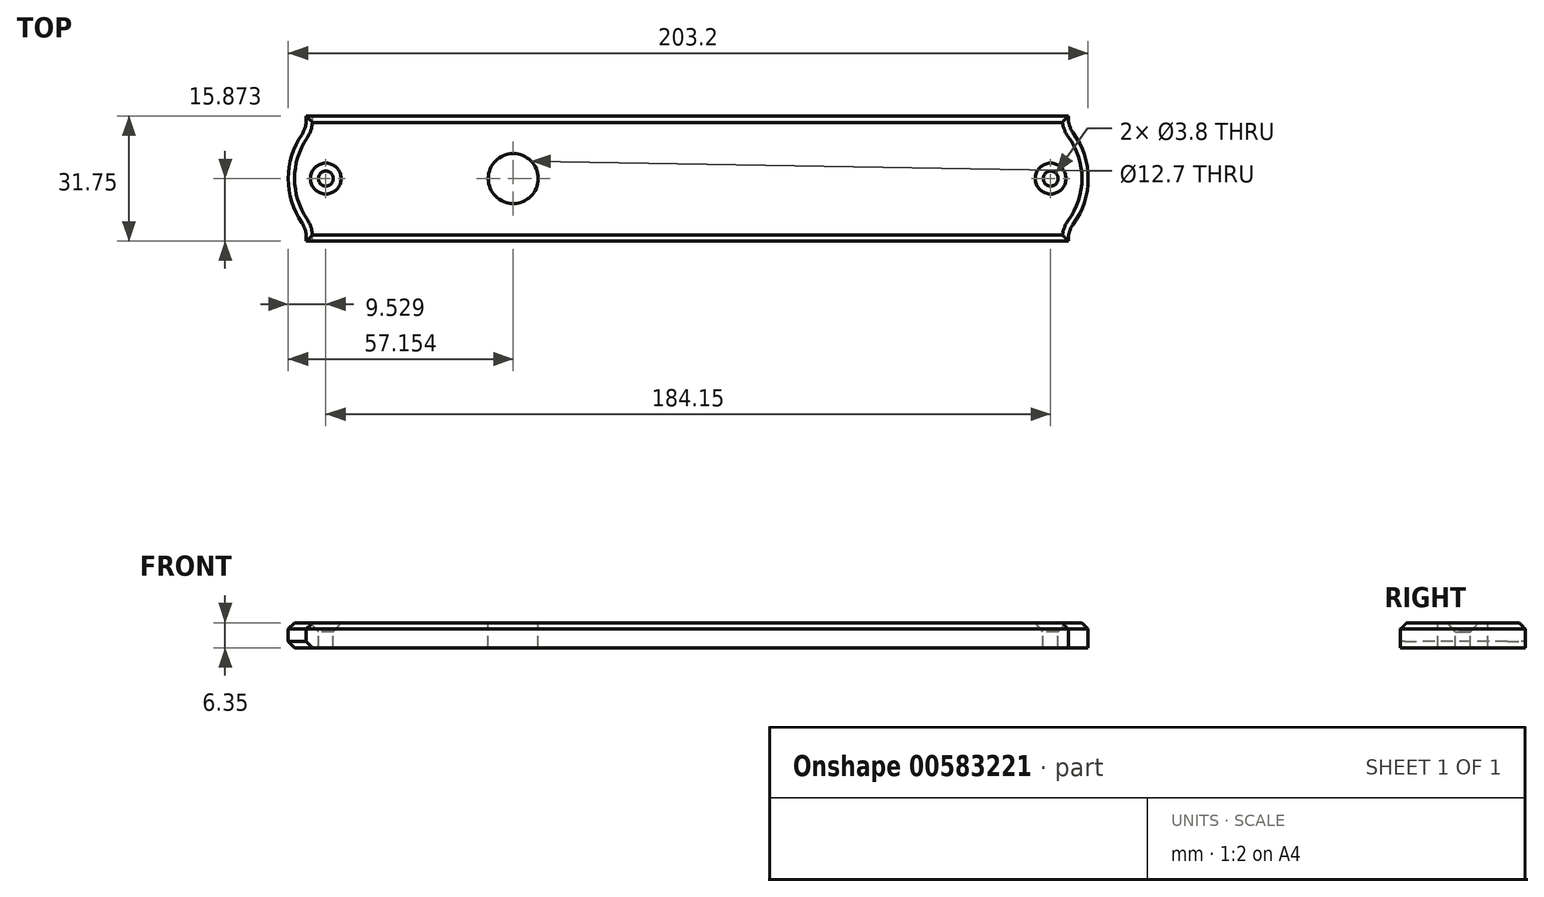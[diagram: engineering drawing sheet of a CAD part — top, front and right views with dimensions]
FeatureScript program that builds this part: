
annotation { "Feature Type Name" : "Feature", "Feature Type Description" : "" }
export const myFeature = defineFeature(function(context is Context, id is Id, definition is map)
    precondition{}
    {
        {
            var Q0;
            Q0=qCreatedBy(makeId("Top.planeOp"),FACE);
            var sketch = newSketch(context, id + "F0", { "sketchPlane" : qUnion([Q0])});
            skLineSegment(sketch, "E0.bottom", {"start": v(-87.1, -14.8) * mm, "end": v(106.53, -14.8) * mm});
            skLineSegment(sketch, "E0.top", {"start": v(-87.1, 16.96) * mm, "end": v(106.53, 16.96) * mm});
            skCircle(sketch, "E1", {"center": v(-34.49, 1.08) * mm, "radius": 6.35 * mm});
            skPoint(sketch, "E1.centerSnap0", {"position": v(-91.64, 1.08) * mm});
            skLineSegment(sketch, "E2", {"start": v(-91.64, 1.08) * mm, "end": v(111.56, 1.08) * mm, "construction": true});
            skPoint(sketch, "E3", {"position": v(-82.11, 9.02) * mm});
            skPoint(sketch, "E4", {"position": v(-82.11, -6.85) * mm});
            skPoint(sketch, "E5", {"position": v(102.04, -6.85) * mm});
            skPoint(sketch, "E6", {"position": v(102.04, 9.02) * mm});
            skPoint(sketch, "E7", {"position": v(-82.11, 1.08) * mm});
            skPoint(sketch, "E8", {"position": v(102.04, 1.08) * mm});
            skLineSegment(sketch, "E9", {"start": v(-87.1, 16.96) * mm, "end": v(-87.1, 15.88) * mm, "construction": true});
            skArc(sketch, "E10", {"start": v(-88.19, 12.32) * mm, "mid": v(-91.64, 1.08) * mm, "end": v(-88.19, -10.15) * mm});
            skLineSegment(sketch, "E11", {"start": v(106.53, 16.96) * mm, "end": v(106.53, 16.48) * mm, "construction": true});
            skArc(sketch, "E12", {"start": v(107.76, -10.56) * mm, "mid": v(111.56, 1.08) * mm, "end": v(107.76, 12.73) * mm});
            skLineSegment(sketch, "E13", {"start": v(-87.1, 16.96) * mm, "end": v(-87.1, 13.78) * mm});
            skLineSegment(sketch, "E14", {"start": v(-87.1, -11.62) * mm, "end": v(-87.1, -14.8) * mm});
            skLineSegment(sketch, "E15", {"start": v(106.53, -12.07) * mm, "end": v(106.53, -14.8) * mm});
            skLineSegment(sketch, "E16", {"start": v(106.53, 14.24) * mm, "end": v(106.53, 16.96) * mm});
            skLineSegment(sketch, "E17.trimOffspring", {"start": v(106.53, -14.31) * mm, "end": v(106.53, -14.8) * mm, "construction": true});
            skLineSegment(sketch, "E18.trimOffspring", {"start": v(-87.1, -13.72) * mm, "end": v(-87.1, -14.8) * mm, "construction": true});
            skPoint(sketch, "E19.orphan", {"position": v(-92.17, 16.96) * mm});
            skPoint(sketch, "E20.orphan", {"position": v(-91.1, -14.8) * mm});
            skPoint(sketch, "E21.orphan", {"position": v(111.61, 16.96) * mm});
            skPoint(sketch, "E22.orphan", {"position": v(111.52, -14.8) * mm});
            skPoint(sketch, "E23.visualSharp", {"position": v(106.53, 14.24) * mm});
            skArc(sketch, "E23.filletArc", {"start": v(106.53, 16.48) * mm, "mid": v(106.85, 14.5) * mm, "end": v(107.76, 12.73) * mm});
            skPoint(sketch, "E24.visualSharp", {"position": v(106.53, -12.07) * mm});
            skArc(sketch, "E24.filletArc", {"start": v(107.76, -10.56) * mm, "mid": v(106.85, -12.34) * mm, "end": v(106.53, -14.31) * mm});
            skPoint(sketch, "E25.visualSharp", {"position": v(-87.1, -11.62) * mm});
            skArc(sketch, "E25.filletArc", {"start": v(-87.1, -13.72) * mm, "mid": v(-87.37, -11.85) * mm, "end": v(-88.19, -10.15) * mm});
            skPoint(sketch, "E26.visualSharp", {"position": v(-87.1, 13.78) * mm});
            skArc(sketch, "E26.filletArc", {"start": v(-88.19, 12.32) * mm, "mid": v(-87.37, 14.02) * mm, "end": v(-87.1, 15.88) * mm});
            skSolve(sketch);
        }
        {
            var Q0;
            Q0 = qSketchRegion(id + "F0", true);
            extrude(context, id + "F1", {"entities" : qUnion([Q0]), "oppositeDirection" : true, "depth" : 6.35 * mm, "offsetDistance" : 25.4 * mm});
        }
        {
            var Q0;
            Q0=sQuery(id+"F0.wireOp",VERTEX,"E8");
            var Q1;
            Q1=sQuery(id+"F0.wireOp",VERTEX,"E7");
            var Q2;
            Q2=makeQuery(id+"F1.opExtrude","SWEPT_BODY",BODY,{"disambiguationData":[OSD([sQuery(id+"F0.wireOp",EDGE,"E0.bottom"),sQuery(id+"F0.wireOp",EDGE,"E0.top"),sQuery(id+"F0.wireOp",EDGE,"E1"),sQuery(id+"F0.wireOp",EDGE,"E10"),sQuery(id+"F0.wireOp",EDGE,"E12"),sQuery(id+"F0.wireOp",EDGE,"E13"),sQuery(id+"F0.wireOp",EDGE,"E14"),sQuery(id+"F0.wireOp",EDGE,"E15"),sQuery(id+"F0.wireOp",EDGE,"E16")])]});
            hole(context, id + "F2", {"style" : HoleStyle.C_SINK, "endStyle" : HoleEndStyle.THROUGH, "standardTappedOrClearance" : lookupTablePath({ "standard" : "ANSI", "fit" : "Normal (ASME)", "size" : "#6", "type" : "Clearance" }), "standardBlindInLast" : lookupTablePath({ "fit" : "Free", "standard" : "ANSI", "size" : "#6", "type" : "Clearance" }), "holeDiameter" : 3.8 * mm, "cSinkDiameter" : 7.8 * mm, "cSinkAngle" : 82 * degree, "majorDiameter" : 6.35 * mm, "tappedDepth" : 15.88 * mm, "tapClearance" : 3, "startFromSketch" : true, "locations" : qUnion([Q0, Q1]), "scope" : qUnion([Q2])});
        }
        {
            var Q0;
            Q0=makeQuery(id+"F1.opExtrude","CAP_EDGE",EDGE,{"disambiguationData":[OSD([sQuery(id+"F0.wireOp",EDGE,"E0.top")])],"isStart":true});
            var Q1;
            Q1=makeQuery(id+"F1.opExtrude","CAP_EDGE",EDGE,{"disambiguationData":[OSD([sQuery(id+"F0.wireOp",EDGE,"E13")])],"isStart":true});
            var Q2;
            Q2=makeQuery(id+"F1.opExtrude","CAP_EDGE",EDGE,{"disambiguationData":[OSD([sQuery(id+"F0.wireOp",EDGE,"E10")])],"isStart":true});
            var Q3;
            Q3=makeQuery(id+"F1.opExtrude","CAP_EDGE",EDGE,{"disambiguationData":[OSD([sQuery(id+"F0.wireOp",EDGE,"E10")])],"isStart":false});
            var Q4;
            Q4=makeQuery(id+"F1.opExtrude","CAP_EDGE",EDGE,{"disambiguationData":[OSD([sQuery(id+"F0.wireOp",EDGE,"E0.bottom")])],"isStart":true});
            var Q5;
            Q5=makeQuery(id+"F1.opExtrude","CAP_EDGE",EDGE,{"disambiguationData":[OSD([sQuery(id+"F0.wireOp",EDGE,"E14")])],"isStart":true});
            var Q6;
            Q6=makeQuery(id+"F1.opExtrude","CAP_EDGE",EDGE,{"disambiguationData":[OSD([sQuery(id+"F0.wireOp",EDGE,"E15")])],"isStart":true});
            var Q7;
            Q7=makeQuery(id+"F1.opExtrude","CAP_EDGE",EDGE,{"disambiguationData":[OSD([sQuery(id+"F0.wireOp",EDGE,"E12")])],"isStart":true});
            var Q8;
            Q8=makeQuery(id+"F1.opExtrude","CAP_EDGE",EDGE,{"disambiguationData":[OSD([sQuery(id+"F0.wireOp",EDGE,"E16")])],"isStart":true});
            chamfer(context, id + "F3", {"entities" : qUnion([Q0, Q1, Q2, Q3, Q4, Q5, Q6, Q7, Q8]), "width" : 1.59 * mm, "tangentPropagation" : true});
        }
    });
